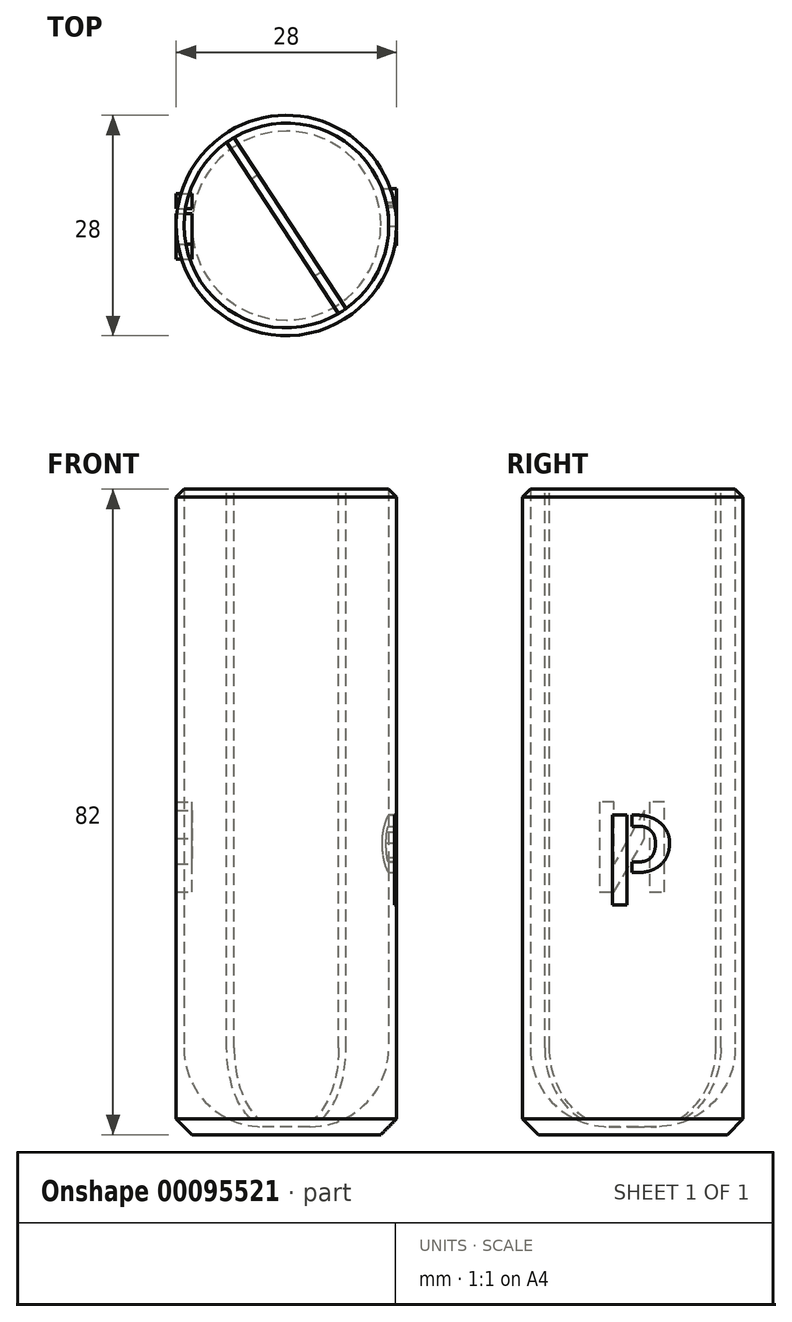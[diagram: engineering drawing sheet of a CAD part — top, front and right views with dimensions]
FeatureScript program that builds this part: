
annotation { "Feature Type Name" : "Feature", "Feature Type Description" : "" }
export const myFeature = defineFeature(function(context is Context, id is Id, definition is map)
    precondition{}
    {
        {
            var Q0;
            Q0=qCreatedBy(makeId("Top.planeOp"),FACE);
            var sketch = newSketch(context, id + "F0", { "sketchPlane" : qUnion([Q0])});
            skCircle(sketch, "E0", {"center": v(0, 0) * mm, "radius": 14 * mm});
            skSolve(sketch);
        }
        {
            var Q0;
            Q0 = qSketchRegion(id + "F0", true);
            extrude(context, id + "F1", {"entities" : qUnion([Q0]), "depth" : 82 * mm});
        }
        {
            var Q0;
            Q0=makeQuery(id+"F1.opExtrude","CAP_FACE",FACE,{"disambiguationData":[OSD([sQuery(id+"F0.wireOp",EDGE,"E0")])],"isStart":false});
            shell(context, id + "F2", {"entities" : qUnion([Q0]), "thickness" : 1 * mm});
        }
        {
            var Q0;
            {var subQ0=sQuery(id+"F0.wireOp",EDGE,"E0");Q0=makeQuery(id+"F2.opShell","OFFSET_EDGE",EDGE,{"disambiguationData":[OSD([subQ0]),TDD([makeQuery(id+"F1.opExtrude","CAP_EDGE",EDGE,{"disambiguationData":[OSD([subQ0])],"isStart":true})])]});}
            fillet(context, id + "F3", {"entities" : qUnion([Q0]), "radius" : 10 * mm, "tangentPropagation" : true, "allowEdgeOverflow" : false});
        }
        {
            var Q0;
            Q0=makeQuery(id+"F1.opExtrude","CAP_EDGE",EDGE,{"disambiguationData":[OSD([sQuery(id+"F0.wireOp",EDGE,"E0")])],"isStart":true});
            chamfer(context, id + "F4", {"entities" : qUnion([Q0]), "width" : 2 * mm, "tangentPropagation" : true});
        }
        {
            var Q0;
            Q0=makeQuery(id+"F1.opExtrude","CAP_FACE",FACE,{"disambiguationData":[OSD([sQuery(id+"F0.wireOp",EDGE,"E0")])],"isStart":false});
            var sketch = newSketch(context, id + "F5", { "sketchPlane" : qUnion([Q0])});
            skLineSegment(sketch, "E1", {"start": v(-7.58, 10.56) * mm, "end": v(6.63, -11.18) * mm});
            skLineSegment(sketch, "E2", {"start": v(7.58, -10.56) * mm, "end": v(-6.63, 11.18) * mm});
            skSolve(sketch);
        }
        {
            var Q0;
            {var subQ0=sQuery(id+"F5.wireOp",EDGE,"E1");Q0=makeQuery(id+"F5.imprint","IMPRINT",FACE,{"disambiguationData":[TD([[makeQuery(id+"F5.imprint","IMPRINT",EDGE,{"derivedFrom":subQ0}),1.0]])]});}
            extrude(context, id + "F6", {"entities" : qUnion([Q0]), "operationType" : NewBodyOperationType.ADD, "oppositeDirection" : true, "depth" : 80 * mm});
        }
        {
            var Q0;
            Q0=makeQuery(id+"F1.opExtrude","CAP_EDGE",EDGE,{"disambiguationData":[OSD([sQuery(id+"F0.wireOp",EDGE,"E0")])],"isStart":false});
            chamfer(context, id + "F7", {"entities" : qUnion([Q0]), "width" : 1 * mm, "tangentPropagation" : true});
        }
        {
            var Q0;
            Q0=qCreatedBy(makeId("Right.planeOp"),FACE);
            cPlane(context, id + "F8", {"entities" : qUnion([Q0]), "cplaneType" : CPlaneType.OFFSET, "offset" : 14 * mm, "width" : 150 * mm, "height" : 150 * mm});
        }
        {
            var Q0;
            Q0=qCreatedBy(id+"F8.planeOp",FACE);
            var sketch = newSketch(context, id + "F9", { "sketchPlane" : qUnion([Q0])});
            skText(sketch, "E3", { "text": "P", "fontName": "AllertaStencil-Regular.ttf"});
            const initialGuessF9  = {"E3": [-0.00398, 0.02919, 1, 0, 0.0114]};
            skSetInitialGuess(sketch, initialGuessF9);
            skSolve(sketch);
        }
        {
            var Q0;
            Q0 = qSketchRegion(id + "F9", true);
            var Q1;
            Q1=makeQuery(id+"F1.opExtrude","SWEPT_BODY",BODY,{"disambiguationData":[OSD([sQuery(id+"F0.wireOp",EDGE,"E0")])]});
            extrude(context, id + "F10", {"entities" : qUnion([Q0]), "endBound" : BoundingType.UP_TO_NEXT, "oppositeDirection" : true, "endBoundEntityBody" : qUnion([Q1]), "depth" : 10 * mm});
        }
        {
            var Q0;
            Q0=qCreatedBy(makeId("Right.planeOp"),FACE);
            cPlane(context, id + "F11", {"entities" : qUnion([Q0]), "cplaneType" : CPlaneType.OFFSET, "offset" : 14 * mm, "oppositeDirection" : true, "width" : 150 * mm, "height" : 150 * mm});
        }
        {
            var Q0;
            Q0=qCreatedBy(id+"F11.planeOp",FACE);
            var sketch = newSketch(context, id + "F12", { "sketchPlane" : qUnion([Q0])});
            skText(sketch, "E4", { "text": "N", "fontName": "AllertaStencil-Regular.ttf"});
            const initialGuessF12  = {"E4": [-0.0059, 0.04083, 1, 0, 0.01147]};
            skSetInitialGuess(sketch, initialGuessF12);
            skSolve(sketch);
        }
        {
            var Q0;
            Q0=makeQuery(id+"F12.imprint","IMPRINT",FACE,{"disambiguationData":[TD([[makeQuery(id+"F12.imprint","IMPRINT",EDGE,{"derivedFrom":sQuery(id+"F12.wireOp",EDGE,"E4.sketch_text.stroke-0")}),-1.0]])]});
            var Q1;
            Q1=makeQuery(id+"F12.imprint","IMPRINT",FACE,{"disambiguationData":[TD([[makeQuery(id+"F12.imprint","IMPRINT",EDGE,{"derivedFrom":sQuery(id+"F12.wireOp",EDGE,"E4.sketch_text.stroke-7")}),-1.0]])]});
            var Q2;
            Q2=makeQuery(id+"F1.opExtrude","SWEPT_FACE",FACE,{"disambiguationData":[OSD([sQuery(id+"F0.wireOp",EDGE,"E0")])]});
            var Q3;
            Q3=makeQuery(id+"F1.opExtrude","SWEPT_BODY",BODY,{"disambiguationData":[OSD([sQuery(id+"F0.wireOp",EDGE,"E0")])]});
            extrude(context, id + "F13", {"entities" : qUnion([Q0, Q1]), "endBoundEntityFace" : qUnion([Q2]), "endBoundEntityBody" : qUnion([Q3]), "depth" : 2 * mm});
        }
        {
            var Q0;
            Q0=makeQuery(id+"F13.opExtrude","SWEPT_BODY",BODY,{"disambiguationData":[OSD([sQuery(id+"F12.wireOp",EDGE,"E4.sketch_text.stroke-0"),sQuery(id+"F12.wireOp",EDGE,"E4.sketch_text.stroke-1"),sQuery(id+"F12.wireOp",EDGE,"E4.sketch_text.stroke-2"),sQuery(id+"F12.wireOp",EDGE,"E4.sketch_text.stroke-3"),sQuery(id+"F12.wireOp",EDGE,"E4.sketch_text.stroke-4"),sQuery(id+"F12.wireOp",EDGE,"E4.sketch_text.stroke-5"),sQuery(id+"F12.wireOp",EDGE,"E4.sketch_text.stroke-6")])]});
            var Q1;
            Q1=makeQuery(id+"F13.opExtrude","SWEPT_BODY",BODY,{"disambiguationData":[OSD([sQuery(id+"F12.wireOp",EDGE,"E4.sketch_text.stroke-7"),sQuery(id+"F12.wireOp",EDGE,"E4.sketch_text.stroke-8"),sQuery(id+"F12.wireOp",EDGE,"E4.sketch_text.stroke-9"),sQuery(id+"F12.wireOp",EDGE,"E4.sketch_text.stroke-10")])]});
            var Q2;
            Q2=makeQuery(id+"F13.opExtrude","CAP_EDGE",EDGE,{"disambiguationData":[OSD([sQuery(id+"F12.wireOp",EDGE,"E4.sketch_text.stroke-7")])],"isStart":true});
            transform(context, id + "F14", {"entities" : qUnion([Q0, Q1]), "transformType" : TransformType.ROTATION, "transformAxis" : qUnion([Q2]), "angle" : 180 * degree, "makeCopy" : false});
        }
        {
            var Q0;
            Q0=makeQuery(id+"F13.opExtrude","SWEPT_BODY",BODY,{"disambiguationData":[OSD([sQuery(id+"F12.wireOp",EDGE,"E4.sketch_text.stroke-7"),sQuery(id+"F12.wireOp",EDGE,"E4.sketch_text.stroke-8"),sQuery(id+"F12.wireOp",EDGE,"E4.sketch_text.stroke-9"),sQuery(id+"F12.wireOp",EDGE,"E4.sketch_text.stroke-10")])]});
            var Q1;
            Q1=makeQuery(id+"F13.opExtrude","SWEPT_BODY",BODY,{"disambiguationData":[OSD([sQuery(id+"F12.wireOp",EDGE,"E4.sketch_text.stroke-0"),sQuery(id+"F12.wireOp",EDGE,"E4.sketch_text.stroke-1"),sQuery(id+"F12.wireOp",EDGE,"E4.sketch_text.stroke-2"),sQuery(id+"F12.wireOp",EDGE,"E4.sketch_text.stroke-3"),sQuery(id+"F12.wireOp",EDGE,"E4.sketch_text.stroke-4"),sQuery(id+"F12.wireOp",EDGE,"E4.sketch_text.stroke-5"),sQuery(id+"F12.wireOp",EDGE,"E4.sketch_text.stroke-6")])]});
            transform(context, id + "F15", {"entities" : qUnion([Q0, Q1]), "transformType" : TransformType.TRANSLATION_3D, "dx" : 2 * mm, "dy" : 8.5 * mm, "dz" : 0 * mm, "makeCopy" : false});
        }
        {
            var Q0;
            Q0=makeQuery(id+"F13.opExtrude","SWEPT_BODY",BODY,{"disambiguationData":[OSD([sQuery(id+"F12.wireOp",EDGE,"E4.sketch_text.stroke-7"),sQuery(id+"F12.wireOp",EDGE,"E4.sketch_text.stroke-8"),sQuery(id+"F12.wireOp",EDGE,"E4.sketch_text.stroke-9"),sQuery(id+"F12.wireOp",EDGE,"E4.sketch_text.stroke-10")])]});
            var Q1;
            Q1=makeQuery(id+"F13.opExtrude","SWEPT_BODY",BODY,{"disambiguationData":[OSD([sQuery(id+"F12.wireOp",EDGE,"E4.sketch_text.stroke-0"),sQuery(id+"F12.wireOp",EDGE,"E4.sketch_text.stroke-1"),sQuery(id+"F12.wireOp",EDGE,"E4.sketch_text.stroke-2"),sQuery(id+"F12.wireOp",EDGE,"E4.sketch_text.stroke-3"),sQuery(id+"F12.wireOp",EDGE,"E4.sketch_text.stroke-4"),sQuery(id+"F12.wireOp",EDGE,"E4.sketch_text.stroke-5"),sQuery(id+"F12.wireOp",EDGE,"E4.sketch_text.stroke-6")])]});
            transform(context, id + "F16", {"entities" : qUnion([Q0, Q1]), "transformType" : TransformType.TRANSLATION_3D, "dx" : 0 * mm, "dy" : 0 * mm, "dz" : -10 * mm, "makeCopy" : false});
        }
    });
